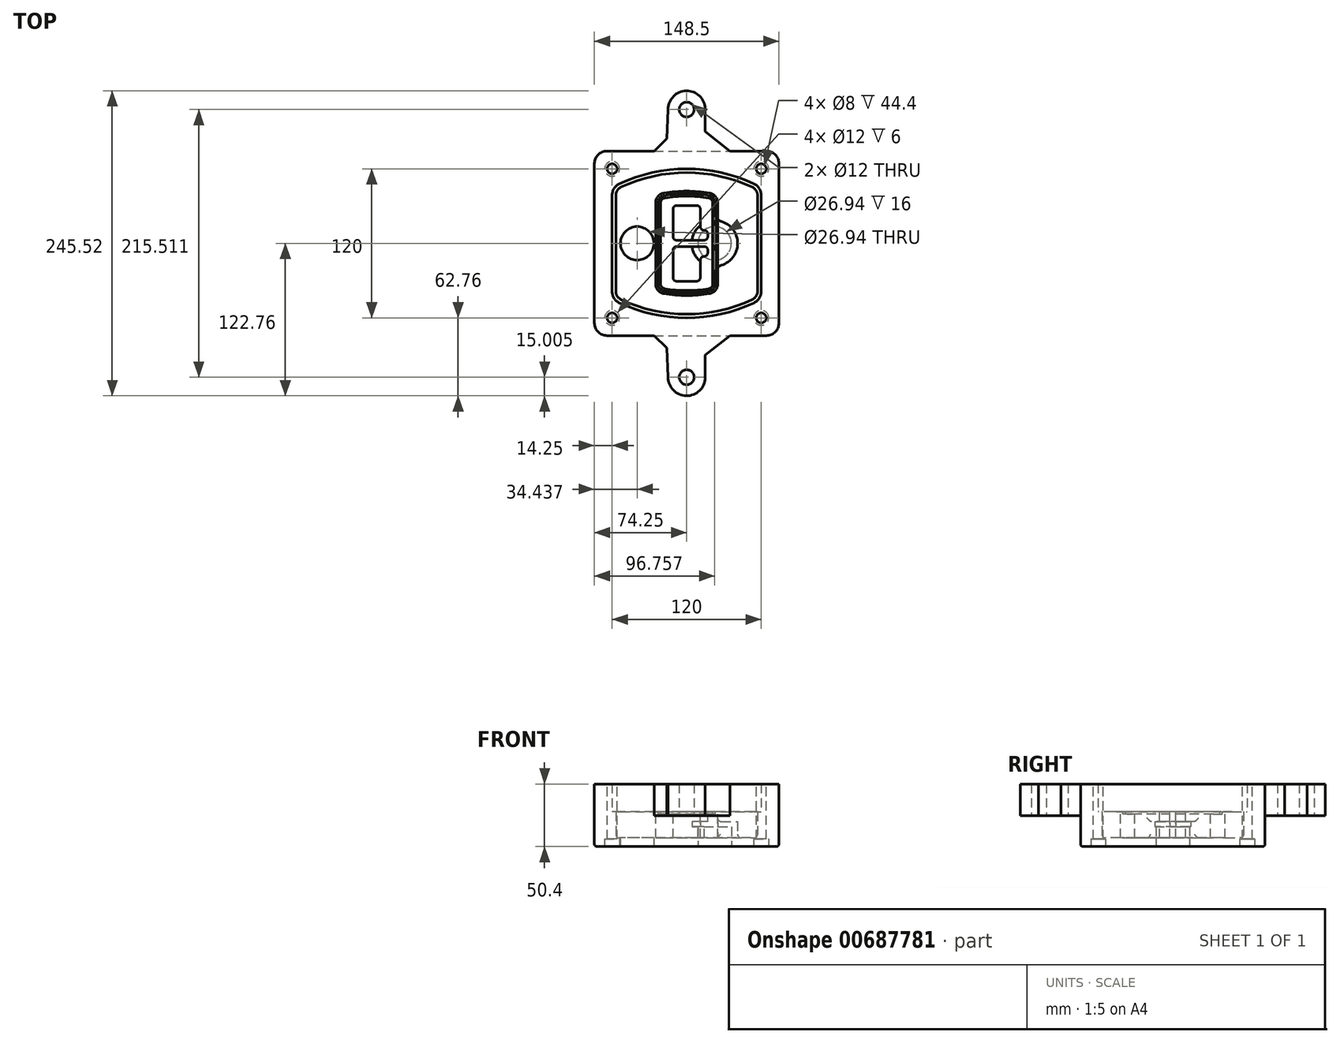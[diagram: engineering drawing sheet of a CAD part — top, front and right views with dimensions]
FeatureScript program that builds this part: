
annotation { "Feature Type Name" : "Feature", "Feature Type Description" : "" }
export const myFeature = defineFeature(function(context is Context, id is Id, definition is map)
    precondition{}
    {
        {
            var Q0;
            Q0=qCreatedBy(makeId("Top.planeOp"),FACE);
            var sketch = newSketch(context, id + "F0", { "sketchPlane" : qUnion([Q0])});
            skPoint(sketch, "E0.rect.middle", {"position": v(0, 0) * mm});
            skLineSegment(sketch, "E1.bottom", {"start": v(-64.25, -74.25) * mm, "end": v(64.25, -74.25) * mm});
            skLineSegment(sketch, "E1.top", {"start": v(-64.25, 74.25) * mm, "end": v(64.25, 74.25) * mm});
            skLineSegment(sketch, "E1.left", {"start": v(-74.25, -64.25) * mm, "end": v(-74.25, 64.25) * mm});
            skLineSegment(sketch, "E1.right", {"start": v(74.25, -64.25) * mm, "end": v(74.25, 64.25) * mm});
            skLineSegment(sketch, "E2", {"start": v(-74.25, 74.25) * mm, "end": v(74.25, -74.25) * mm, "construction": true});
            skLineSegment(sketch, "E3", {"start": v(74.25, 74.25) * mm, "end": v(-74.25, -74.25) * mm, "construction": true});
            skCircle(sketch, "E4", {"center": v(-60, 60) * mm, "radius": 4 * mm});
            skCircle(sketch, "E5", {"center": v(60, 60) * mm, "radius": 4 * mm});
            skCircle(sketch, "E6", {"center": v(60, -60) * mm, "radius": 4 * mm});
            skCircle(sketch, "E7", {"center": v(-60, -60) * mm, "radius": 4 * mm});
            skLineSegment(sketch, "E8", {"start": v(-60, 60) * mm, "end": v(60, 60) * mm, "construction": true});
            skLineSegment(sketch, "E9", {"start": v(60, 60) * mm, "end": v(60, -60) * mm, "construction": true});
            skLineSegment(sketch, "E10", {"start": v(60, -60) * mm, "end": v(-60, -60) * mm, "construction": true});
            skLineSegment(sketch, "E11", {"start": v(-60, -60) * mm, "end": v(-60, 60) * mm, "construction": true});
            skLineSegment(sketch, "E12", {"start": v(-60, 38.83) * mm, "end": v(-60, -38.83) * mm});
            skLineSegment(sketch, "E13", {"start": v(60, 38.83) * mm, "end": v(60, -38.83) * mm});
            skArc(sketch, "E14", {"start": v(54.26, 47.88) * mm, "mid": v(0, 60) * mm, "end": v(-54.26, 47.88) * mm});
            skArc(sketch, "E15", {"start": v(-54.26, -47.88) * mm, "mid": v(0, -60) * mm, "end": v(54.26, -47.88) * mm});
            skLineSegment(sketch, "E16", {"start": v(-60, 0) * mm, "end": v(60, 0) * mm, "construction": true});
            skPoint(sketch, "E17.visualSharp", {"position": v(-60, -45) * mm});
            skArc(sketch, "E17.filletArc", {"start": v(-60, -38.83) * mm, "mid": v(-58.44, -44.2) * mm, "end": v(-54.26, -47.88) * mm});
            skPoint(sketch, "E18.visualSharp", {"position": v(-60, 45) * mm});
            skArc(sketch, "E18.filletArc", {"start": v(-54.26, 47.88) * mm, "mid": v(-58.44, 44.2) * mm, "end": v(-60, 38.83) * mm});
            skPoint(sketch, "E19.visualSharp", {"position": v(60, 45) * mm});
            skArc(sketch, "E19.filletArc", {"start": v(60, 38.83) * mm, "mid": v(58.44, 44.2) * mm, "end": v(54.26, 47.88) * mm});
            skPoint(sketch, "E20.visualSharp", {"position": v(60, -45) * mm});
            skArc(sketch, "E20.filletArc", {"start": v(54.26, -47.88) * mm, "mid": v(58.44, -44.2) * mm, "end": v(60, -38.83) * mm});
            skPoint(sketch, "E21.visualSharp", {"position": v(-74.25, 74.25) * mm});
            skArc(sketch, "E21.filletArc", {"start": v(-64.25, 74.25) * mm, "mid": v(-71.32, 71.32) * mm, "end": v(-74.25, 64.25) * mm});
            skPoint(sketch, "E22.visualSharp", {"position": v(74.25, 74.25) * mm});
            skArc(sketch, "E22.filletArc", {"start": v(74.25, 64.25) * mm, "mid": v(71.32, 71.32) * mm, "end": v(64.25, 74.25) * mm});
            skPoint(sketch, "E23.visualSharp", {"position": v(74.25, -74.25) * mm});
            skArc(sketch, "E23.filletArc", {"start": v(64.25, -74.25) * mm, "mid": v(71.32, -71.32) * mm, "end": v(74.25, -64.25) * mm});
            skPoint(sketch, "E24.visualSharp", {"position": v(-74.25, -74.25) * mm});
            skArc(sketch, "E24.filletArc", {"start": v(-74.25, -64.25) * mm, "mid": v(-71.32, -71.32) * mm, "end": v(-64.25, -74.25) * mm});
            skArc(sketch, "E25.0", {"start": v(57, 38.83) * mm, "mid": v(55.9, 42.58) * mm, "end": v(52.98, 45.17) * mm});
            skLineSegment(sketch, "E25.1", {"start": v(57, 38.83) * mm, "end": v(57, -38.83) * mm});
            skArc(sketch, "E25.2", {"start": v(52.98, -45.17) * mm, "mid": v(55.9, -42.58) * mm, "end": v(57, -38.83) * mm});
            skArc(sketch, "E25.3", {"start": v(-52.98, -45.17) * mm, "mid": v(0, -57) * mm, "end": v(52.98, -45.17) * mm});
            skArc(sketch, "E25.4", {"start": v(-57, -38.83) * mm, "mid": v(-55.9, -42.58) * mm, "end": v(-52.98, -45.17) * mm});
            skArc(sketch, "E25.5", {"start": v(52.98, 45.17) * mm, "mid": v(0, 57) * mm, "end": v(-52.98, 45.17) * mm});
            skLineSegment(sketch, "E25.6", {"start": v(-57, 38.83) * mm, "end": v(-57, -38.83) * mm});
            skArc(sketch, "E25.7", {"start": v(-52.98, 45.17) * mm, "mid": v(-55.9, 42.58) * mm, "end": v(-57, 38.83) * mm});
            skArc(sketch, "E26.0", {"start": v(-55.96, 51.5) * mm, "mid": v(-61.82, 46.33) * mm, "end": v(-64, 38.83) * mm});
            skArc(sketch, "E26.1", {"start": v(55.96, 51.5) * mm, "mid": v(0, 64) * mm, "end": v(-55.96, 51.5) * mm});
            skArc(sketch, "E26.2", {"start": v(64, 38.83) * mm, "mid": v(61.82, 46.33) * mm, "end": v(55.96, 51.5) * mm});
            skLineSegment(sketch, "E26.3", {"start": v(64, 38.83) * mm, "end": v(64, -38.83) * mm});
            skArc(sketch, "E26.4", {"start": v(55.96, -51.5) * mm, "mid": v(61.82, -46.33) * mm, "end": v(64, -38.83) * mm});
            skLineSegment(sketch, "E26.5", {"start": v(-64, 38.83) * mm, "end": v(-64, -38.83) * mm});
            skArc(sketch, "E26.6", {"start": v(-55.96, -51.5) * mm, "mid": v(0, -64) * mm, "end": v(55.96, -51.5) * mm});
            skArc(sketch, "E26.7", {"start": v(-64, -38.83) * mm, "mid": v(-61.82, -46.33) * mm, "end": v(-55.96, -51.5) * mm});
            skSolve(sketch);
        }
        {
            var Q0;
            Q0=makeQuery(id+"F0.imprint","IMPRINT",FACE,{"disambiguationData":[TD([[makeQuery(id+"F0.imprint","IMPRINT",EDGE,{"derivedFrom":sQuery(id+"F0.wireOp",EDGE,"E1.bottom")}),1.0]])]});
            var Q1;
            Q1=makeQuery(id+"F0.imprint","IMPRINT",FACE,{"disambiguationData":[TD([[makeQuery(id+"F0.imprint","IMPRINT",EDGE,{"derivedFrom":sQuery(id+"F0.wireOp",EDGE,"E12")}),1.0]])]});
            var Q2;
            Q2=makeQuery(id+"F0.imprint","IMPRINT",FACE,{"disambiguationData":[TD([[makeQuery(id+"F0.imprint","IMPRINT",EDGE,{"derivedFrom":sQuery(id+"F0.wireOp",EDGE,"E25.0")}),1.0]])]});
            var Q3;
            Q3=makeQuery(id+"F0.imprint","IMPRINT",FACE,{"disambiguationData":[TD([[makeQuery(id+"F0.imprint","IMPRINT",EDGE,{"derivedFrom":sQuery(id+"F0.wireOp",EDGE,"E12")}),-1.0]])]});
            extrude(context, id + "F1", {"entities" : qUnion([Q0, Q1, Q2, Q3]), "oppositeDirection" : true, "depth" : 25 * mm});
        }
        {
            var Q0;
            Q0=makeQuery(id+"F0.imprint","IMPRINT",FACE,{"disambiguationData":[TD([[makeQuery(id+"F0.imprint","IMPRINT",EDGE,{"derivedFrom":sQuery(id+"F0.wireOp",EDGE,"E12")}),1.0]])]});
            extrude(context, id + "F2", {"entities" : qUnion([Q0]), "operationType" : NewBodyOperationType.ADD, "depth" : 3 * mm});
        }
        {
            var Q0;
            Q0=makeQuery(id+"F0.imprint","IMPRINT",FACE,{"disambiguationData":[TD([[makeQuery(id+"F0.imprint","IMPRINT",EDGE,{"derivedFrom":sQuery(id+"F0.wireOp",EDGE,"E25.0")}),1.0]])]});
            extrude(context, id + "F3", {"entities" : qUnion([Q0]), "operationType" : NewBodyOperationType.REMOVE, "oppositeDirection" : true, "depth" : 18 * mm});
        }
        {
            var Q0;
            Q0=makeQuery(id+"F2.opExtrude","CAP_FACE",FACE,{"disambiguationData":[OSD([sQuery(id+"F0.wireOp",EDGE,"E12"),sQuery(id+"F0.wireOp",EDGE,"E13"),sQuery(id+"F0.wireOp",EDGE,"E14"),sQuery(id+"F0.wireOp",EDGE,"E15"),sQuery(id+"F0.wireOp",EDGE,"E17.filletArc"),sQuery(id+"F0.wireOp",EDGE,"E18.filletArc"),sQuery(id+"F0.wireOp",EDGE,"E19.filletArc"),sQuery(id+"F0.wireOp",EDGE,"E20.filletArc"),sQuery(id+"F0.wireOp",EDGE,"E25.0"),sQuery(id+"F0.wireOp",EDGE,"E25.1"),sQuery(id+"F0.wireOp",EDGE,"E25.2"),sQuery(id+"F0.wireOp",EDGE,"E25.3"),sQuery(id+"F0.wireOp",EDGE,"E25.4"),sQuery(id+"F0.wireOp",EDGE,"E25.5"),sQuery(id+"F0.wireOp",EDGE,"E25.6"),sQuery(id+"F0.wireOp",EDGE,"E25.7")])],"isStart":false});
            var sketch = newSketch(context, id + "F4", { "sketchPlane" : qUnion([Q0])});
            skArc(sketch, "E27.0", {"start": v(-18.34, -40.45) * mm, "mid": v(0, -42) * mm, "end": v(18.34, -40.45) * mm});
            skArc(sketch, "E28.0", {"start": v(18.34, 40.45) * mm, "mid": v(0, 42) * mm, "end": v(-18.34, 40.45) * mm});
            skLineSegment(sketch, "E29", {"start": v(-25, 32.57) * mm, "end": v(-25, -32.57) * mm});
            skLineSegment(sketch, "E30", {"start": v(25, 32.57) * mm, "end": v(25, -32.57) * mm});
            skLineSegment(sketch, "E31", {"start": v(-25, 39.1) * mm, "end": v(25, 39.1) * mm, "construction": true});
            skLineSegment(sketch, "E32", {"start": v(-25, -39.1) * mm, "end": v(25, -39.1) * mm, "construction": true});
            skPoint(sketch, "E33.visualSharp", {"position": v(-25, 39.1) * mm});
            skArc(sketch, "E33.filletArc", {"start": v(-18.34, 40.45) * mm, "mid": v(-23.11, 37.73) * mm, "end": v(-25, 32.57) * mm});
            skPoint(sketch, "E34.visualSharp", {"position": v(25, 39.1) * mm});
            skArc(sketch, "E34.filletArc", {"start": v(25, 32.57) * mm, "mid": v(23.11, 37.73) * mm, "end": v(18.34, 40.45) * mm});
            skPoint(sketch, "E35.visualSharp", {"position": v(25, -39.1) * mm});
            skArc(sketch, "E35.filletArc", {"start": v(18.34, -40.45) * mm, "mid": v(23.11, -37.73) * mm, "end": v(25, -32.57) * mm});
            skPoint(sketch, "E36.visualSharp", {"position": v(-25, -39.1) * mm});
            skArc(sketch, "E36.filletArc", {"start": v(-25, -32.57) * mm, "mid": v(-23.11, -37.73) * mm, "end": v(-18.34, -40.45) * mm});
            skArc(sketch, "E37.0", {"start": v(52.98, 45.17) * mm, "mid": v(0, 57) * mm, "end": v(-52.98, 45.17) * mm});
            skArc(sketch, "E37.1", {"start": v(-52.98, 45.17) * mm, "mid": v(-55.9, 42.58) * mm, "end": v(-57, 38.83) * mm});
            skLineSegment(sketch, "E37.2", {"start": v(-57, 38.83) * mm, "end": v(-57, -38.83) * mm});
            skArc(sketch, "E37.3", {"start": v(-57, -38.83) * mm, "mid": v(-55.9, -42.58) * mm, "end": v(-52.98, -45.17) * mm});
            skArc(sketch, "E37.4", {"start": v(-52.98, -45.17) * mm, "mid": v(0, -57) * mm, "end": v(52.98, -45.17) * mm});
            skArc(sketch, "E37.5", {"start": v(52.98, -45.17) * mm, "mid": v(55.9, -42.58) * mm, "end": v(57, -38.83) * mm});
            skLineSegment(sketch, "E37.6", {"start": v(57, 38.83) * mm, "end": v(57, -38.83) * mm});
            skArc(sketch, "E37.7", {"start": v(57, 38.83) * mm, "mid": v(55.9, 42.58) * mm, "end": v(52.98, 45.17) * mm});
            skLineSegment(sketch, "E38.0", {"start": v(23, 32.57) * mm, "end": v(23, -32.57) * mm});
            skArc(sketch, "E38.1", {"start": v(18, -38.48) * mm, "mid": v(21.58, -36.44) * mm, "end": v(23, -32.57) * mm});
            skArc(sketch, "E38.2", {"start": v(-18, -38.48) * mm, "mid": v(0, -40) * mm, "end": v(18, -38.48) * mm});
            skArc(sketch, "E38.3", {"start": v(-23, -32.57) * mm, "mid": v(-21.58, -36.44) * mm, "end": v(-18, -38.48) * mm});
            skLineSegment(sketch, "E38.4", {"start": v(-23, 32.57) * mm, "end": v(-23, -32.57) * mm});
            skArc(sketch, "E38.5", {"start": v(23, 32.57) * mm, "mid": v(21.58, 36.44) * mm, "end": v(18, 38.48) * mm});
            skArc(sketch, "E38.6", {"start": v(-18, 38.48) * mm, "mid": v(-21.58, 36.44) * mm, "end": v(-23, 32.57) * mm});
            skArc(sketch, "E38.7", {"start": v(18, 38.48) * mm, "mid": v(0, 40) * mm, "end": v(-18, 38.48) * mm});
            skArc(sketch, "E39.0", {"start": v(21, 32.57) * mm, "mid": v(20.06, 35.15) * mm, "end": v(17.67, 36.5) * mm});
            skLineSegment(sketch, "E39.1", {"start": v(21, 32.57) * mm, "end": v(21, -32.57) * mm});
            skArc(sketch, "E39.2", {"start": v(17.67, -36.5) * mm, "mid": v(20.06, -35.15) * mm, "end": v(21, -32.57) * mm});
            skArc(sketch, "E39.3", {"start": v(-17.67, -36.5) * mm, "mid": v(0, -38) * mm, "end": v(17.67, -36.5) * mm});
            skArc(sketch, "E39.4", {"start": v(-21, -32.57) * mm, "mid": v(-20.06, -35.15) * mm, "end": v(-17.67, -36.5) * mm});
            skArc(sketch, "E39.5", {"start": v(17.67, 36.5) * mm, "mid": v(0, 38) * mm, "end": v(-17.67, 36.5) * mm});
            skLineSegment(sketch, "E39.6", {"start": v(-21, 32.57) * mm, "end": v(-21, -32.57) * mm});
            skArc(sketch, "E39.7", {"start": v(-17.67, 36.5) * mm, "mid": v(-20.06, 35.15) * mm, "end": v(-21, 32.57) * mm});
            skLineSegment(sketch, "E40", {"start": v(-25, 0) * mm, "end": v(25, 0) * mm, "construction": true});
            skLineSegment(sketch, "E41", {"start": v(-11, 5.5) * mm, "end": v(-11, 27.5) * mm});
            skLineSegment(sketch, "E42", {"start": v(-8, 30.5) * mm, "end": v(8, 30.5) * mm});
            skLineSegment(sketch, "E43", {"start": v(11, 27.5) * mm, "end": v(11, 13.5) * mm});
            skLineSegment(sketch, "E44", {"start": v(14, 10.5) * mm, "end": v(14, 10.5) * mm});
            skLineSegment(sketch, "E45", {"start": v(17, 7.5) * mm, "end": v(17, 5.5) * mm});
            skLineSegment(sketch, "E46", {"start": v(14, 2.5) * mm, "end": v(-8, 2.5) * mm});
            skPoint(sketch, "E47.visualSharp", {"position": v(-11, 30.5) * mm});
            skArc(sketch, "E47.filletArc", {"start": v(-8, 30.5) * mm, "mid": v(-10.12, 29.62) * mm, "end": v(-11, 27.5) * mm});
            skPoint(sketch, "E48.visualSharp", {"position": v(11, 30.5) * mm});
            skArc(sketch, "E48.filletArc", {"start": v(11, 27.5) * mm, "mid": v(10.12, 29.62) * mm, "end": v(8, 30.5) * mm});
            skPoint(sketch, "E49.visualSharp", {"position": v(11, 10.5) * mm});
            skArc(sketch, "E49.filletArc", {"start": v(11, 13.5) * mm, "mid": v(11.88, 11.38) * mm, "end": v(14, 10.5) * mm});
            skPoint(sketch, "E50.visualSharp", {"position": v(17, 10.5) * mm});
            skArc(sketch, "E50.filletArc", {"start": v(17, 7.5) * mm, "mid": v(16.12, 9.62) * mm, "end": v(14, 10.5) * mm});
            skPoint(sketch, "E51.visualSharp", {"position": v(17, 2.5) * mm});
            skArc(sketch, "E51.filletArc", {"start": v(14, 2.5) * mm, "mid": v(16.12, 3.38) * mm, "end": v(17, 5.5) * mm});
            skPoint(sketch, "E52.visualSharp", {"position": v(-11, 2.5) * mm});
            skArc(sketch, "E52.filletArc", {"start": v(-11, 5.5) * mm, "mid": v(-10.12, 3.38) * mm, "end": v(-8, 2.5) * mm});
            skLineSegment(sketch, "E53.0.MirrorCS", {"start": v(14, -2.5) * mm, "end": v(-8, -2.5) * mm});
            skArc(sketch, "E54.0.MirrorCS", {"start": v(-11, -5.5) * mm, "mid": v(-10.12, -3.38) * mm, "end": v(-8, -2.5) * mm});
            skLineSegment(sketch, "E55.0.MirrorCS", {"start": v(-11, -5.5) * mm, "end": v(-11, -27.5) * mm});
            skArc(sketch, "E56.0.MirrorCS", {"start": v(-8, -30.5) * mm, "mid": v(-10.12, -29.62) * mm, "end": v(-11, -27.5) * mm});
            skLineSegment(sketch, "E57.0.MirrorCS", {"start": v(-8, -30.5) * mm, "end": v(8, -30.5) * mm});
            skArc(sketch, "E58.0.MirrorCS", {"start": v(11, -27.5) * mm, "mid": v(10.12, -29.62) * mm, "end": v(8, -30.5) * mm});
            skLineSegment(sketch, "E59.0.MirrorCS", {"start": v(11, -27.5) * mm, "end": v(11, -13.5) * mm});
            skArc(sketch, "E60.0.MirrorCS", {"start": v(11, -13.5) * mm, "mid": v(11.88, -11.38) * mm, "end": v(14, -10.5) * mm});
            skArc(sketch, "E61.0.MirrorCS", {"start": v(17, -7.5) * mm, "mid": v(16.12, -9.62) * mm, "end": v(14, -10.5) * mm});
            skLineSegment(sketch, "E62.0.MirrorCS", {"start": v(17, -7.5) * mm, "end": v(17, -5.5) * mm});
            skArc(sketch, "E63.0.MirrorCS", {"start": v(14, -2.5) * mm, "mid": v(16.12, -3.38) * mm, "end": v(17, -5.5) * mm});
            skSolve(sketch);
        }
        {
            var Q0;
            Q0=makeQuery(id+"F4.imprint","IMPRINT",FACE,{"disambiguationData":[TD([[makeQuery(id+"F4.imprint","IMPRINT",EDGE,{"derivedFrom":sQuery(id+"F4.wireOp",EDGE,"E27.0")}),1.0]])]});
            var Q1;
            Q1=makeQuery(id+"F4.imprint","IMPRINT",FACE,{"disambiguationData":[TD([[makeQuery(id+"F4.imprint","IMPRINT",EDGE,{"derivedFrom":sQuery(id+"F4.wireOp",EDGE,"E38.0")}),-1.0]])]});
            var Q2;
            Q2=makeQuery(id+"F4.imprint","IMPRINT",FACE,{"disambiguationData":[TD([[makeQuery(id+"F4.imprint","IMPRINT",EDGE,{"derivedFrom":sQuery(id+"F4.wireOp",EDGE,"E39.0")}),1.0]])]});
            extrude(context, id + "F5", {"entities" : qUnion([Q0, Q1, Q2]), "operationType" : NewBodyOperationType.ADD, "endBound" : BoundingType.UP_TO_NEXT, "oppositeDirection" : true, "depth" : 25 * mm});
        }
        {
            var Q0;
            Q0=makeQuery(id+"F4.imprint","IMPRINT",FACE,{"disambiguationData":[TD([[makeQuery(id+"F4.imprint","IMPRINT",EDGE,{"derivedFrom":sQuery(id+"F4.wireOp",EDGE,"E38.0")}),-1.0]])]});
            extrude(context, id + "F6", {"entities" : qUnion([Q0]), "operationType" : NewBodyOperationType.REMOVE, "oppositeDirection" : true, "depth" : 2 * mm});
        }
        {
            var Q0;
            Q0=makeQuery(id+"F1.opExtrude","CAP_FACE",FACE,{"disambiguationData":[OSD([sQuery(id+"F0.wireOp",EDGE,"E1.bottom"),sQuery(id+"F0.wireOp",EDGE,"E1.top"),sQuery(id+"F0.wireOp",EDGE,"E1.left"),sQuery(id+"F0.wireOp",EDGE,"E1.right"),sQuery(id+"F0.wireOp",EDGE,"E4"),sQuery(id+"F0.wireOp",EDGE,"E5"),sQuery(id+"F0.wireOp",EDGE,"E6"),sQuery(id+"F0.wireOp",EDGE,"E7"),sQuery(id+"F0.wireOp",EDGE,"E21.filletArc"),sQuery(id+"F0.wireOp",EDGE,"E22.filletArc"),sQuery(id+"F0.wireOp",EDGE,"E23.filletArc"),sQuery(id+"F0.wireOp",EDGE,"E24.filletArc")])],"isStart":false});
            var sketch = newSketch(context, id + "F7", { "sketchPlane" : qUnion([Q0])});
            skCircle(sketch, "E64", {"center": v(22.5, 0) * mm, "radius": 13.47 * mm});
            skCircle(sketch, "E65", {"center": v(-39.81, 0) * mm, "radius": 13.47 * mm});
            skLineSegment(sketch, "E66", {"start": v(74.25, 0) * mm, "end": v(-74.25, 0) * mm});
            skCircle(sketch, "E67", {"center": v(22.5, 0) * mm, "radius": 18.47 * mm});
            skCircle(sketch, "E68", {"center": v(60, -60) * mm, "radius": 6 * mm});
            skCircle(sketch, "E69", {"center": v(-60, -60) * mm, "radius": 6 * mm});
            skCircle(sketch, "E70", {"center": v(-60, 60) * mm, "radius": 6 * mm});
            skCircle(sketch, "E71", {"center": v(60, 60) * mm, "radius": 6 * mm});
            skSolve(sketch);
        }
        {
            var Q0;
            {var subQ1=sQuery(id+"F7.wireOp",EDGE,"E66");var subQ4=sQuery(id+"F7.wireOp",EDGE,"E64");var subQ6=makeQuery(id+"F7.imprint","INTERSECT",VERTEX,{"disambiguationData":[OD(0.0)],"derivedFrom":[subQ4,subQ1]});Q0=makeQuery(id+"F7.imprint","IMPRINT",FACE,{"disambiguationData":[TD([[makeQuery(id+"F7.imprint","IMPRINT",EDGE,{"disambiguationData":[TD([[subQ6,-1.0]])],"derivedFrom":subQ4}),-1.0]])]});}
            var Q1;
            {var subQ0=sQuery(id+"F7.wireOp",EDGE,"E66");var subQ1=sQuery(id+"F7.wireOp",EDGE,"E64");var subQ3=makeQuery(id+"F7.imprint","INTERSECT",VERTEX,{"disambiguationData":[OD(0.0)],"derivedFrom":[subQ1,subQ0]});Q1=makeQuery(id+"F7.imprint","IMPRINT",FACE,{"disambiguationData":[TD([[makeQuery(id+"F7.imprint","IMPRINT",EDGE,{"disambiguationData":[TD([[subQ3,-1.0]])],"derivedFrom":subQ1}),1.0]])]});}
            var Q2;
            {var subQ0=sQuery(id+"F7.wireOp",EDGE,"E66");var subQ1=sQuery(id+"F7.wireOp",EDGE,"E64");var subQ3=makeQuery(id+"F7.imprint","INTERSECT",VERTEX,{"disambiguationData":[OD(0.0)],"derivedFrom":[subQ1,subQ0]});Q2=makeQuery(id+"F7.imprint","IMPRINT",FACE,{"disambiguationData":[TD([[makeQuery(id+"F7.imprint","IMPRINT",EDGE,{"disambiguationData":[TD([[subQ3,1.0]])],"derivedFrom":subQ1}),1.0]])]});}
            var Q3;
            {var subQ1=sQuery(id+"F7.wireOp",EDGE,"E66");var subQ4=sQuery(id+"F7.wireOp",EDGE,"E64");var subQ6=makeQuery(id+"F7.imprint","INTERSECT",VERTEX,{"disambiguationData":[OD(0.0)],"derivedFrom":[subQ4,subQ1]});Q3=makeQuery(id+"F7.imprint","IMPRINT",FACE,{"disambiguationData":[TD([[makeQuery(id+"F7.imprint","IMPRINT",EDGE,{"disambiguationData":[TD([[subQ6,1.0]])],"derivedFrom":subQ4}),-1.0]])]});}
            extrude(context, id + "F8", {"entities" : qUnion([Q0, Q1, Q2, Q3]), "operationType" : NewBodyOperationType.ADD, "oppositeDirection" : true, "depth" : 20 * mm});
        }
        {
            var Q0;
            {var subQ0=sQuery(id+"F7.wireOp",EDGE,"E66");var subQ1=sQuery(id+"F7.wireOp",EDGE,"E64");var subQ3=makeQuery(id+"F7.imprint","INTERSECT",VERTEX,{"disambiguationData":[OD(0.0)],"derivedFrom":[subQ1,subQ0]});Q0=makeQuery(id+"F7.imprint","IMPRINT",FACE,{"disambiguationData":[TD([[makeQuery(id+"F7.imprint","IMPRINT",EDGE,{"disambiguationData":[TD([[subQ3,-1.0]])],"derivedFrom":subQ1}),1.0]])]});}
            var Q1;
            {var subQ0=sQuery(id+"F7.wireOp",EDGE,"E66");var subQ1=sQuery(id+"F7.wireOp",EDGE,"E64");var subQ3=makeQuery(id+"F7.imprint","INTERSECT",VERTEX,{"disambiguationData":[OD(0.0)],"derivedFrom":[subQ1,subQ0]});Q1=makeQuery(id+"F7.imprint","IMPRINT",FACE,{"disambiguationData":[TD([[makeQuery(id+"F7.imprint","IMPRINT",EDGE,{"disambiguationData":[TD([[subQ3,1.0]])],"derivedFrom":subQ1}),1.0]])]});}
            extrude(context, id + "F9", {"entities" : qUnion([Q0, Q1]), "operationType" : NewBodyOperationType.REMOVE, "oppositeDirection" : true, "depth" : 16 * mm});
        }
        {
            var Q0;
            {var subQ0=sQuery(id+"F7.wireOp",EDGE,"E66");var subQ1=sQuery(id+"F7.wireOp",EDGE,"E65");var subQ3=makeQuery(id+"F7.imprint","INTERSECT",VERTEX,{"disambiguationData":[OD(0.0)],"derivedFrom":[subQ1,subQ0]});Q0=makeQuery(id+"F7.imprint","IMPRINT",FACE,{"disambiguationData":[TD([[makeQuery(id+"F7.imprint","IMPRINT",EDGE,{"disambiguationData":[TD([[subQ3,-1.0]])],"derivedFrom":subQ1}),1.0]])]});}
            var Q1;
            {var subQ0=sQuery(id+"F7.wireOp",EDGE,"E66");var subQ1=sQuery(id+"F7.wireOp",EDGE,"E65");var subQ3=makeQuery(id+"F7.imprint","INTERSECT",VERTEX,{"disambiguationData":[OD(0.0)],"derivedFrom":[subQ1,subQ0]});Q1=makeQuery(id+"F7.imprint","IMPRINT",FACE,{"disambiguationData":[TD([[makeQuery(id+"F7.imprint","IMPRINT",EDGE,{"disambiguationData":[TD([[subQ3,1.0]])],"derivedFrom":subQ1}),1.0]])]});}
            extrude(context, id + "F10", {"entities" : qUnion([Q0, Q1]), "operationType" : NewBodyOperationType.REMOVE, "oppositeDirection" : true, "depth" : 25 * mm});
        }
        {
            var Q0;
            Q0=makeQuery(id+"F7.imprint","IMPRINT",FACE,{"disambiguationData":[TD([[makeQuery(id+"F7.imprint","IMPRINT",EDGE,{"derivedFrom":sQuery(id+"F7.wireOp",EDGE,"E68")}),1.0]])]});
            var Q1;
            Q1=makeQuery(id+"F7.imprint","IMPRINT",FACE,{"disambiguationData":[TD([[makeQuery(id+"F7.imprint","IMPRINT",EDGE,{"derivedFrom":makeQuery(id+"F1.opExtrude","CAP_EDGE",EDGE,{"disambiguationData":[OSD([sQuery(id+"F0.wireOp",EDGE,"E5")])],"isStart":false})}),-1.0]])]});
            var Q2;
            Q2=makeQuery(id+"F7.imprint","IMPRINT",FACE,{"disambiguationData":[TD([[makeQuery(id+"F7.imprint","IMPRINT",EDGE,{"derivedFrom":sQuery(id+"F7.wireOp",EDGE,"E69")}),1.0]])]});
            var Q3;
            Q3=makeQuery(id+"F7.imprint","IMPRINT",FACE,{"disambiguationData":[TD([[makeQuery(id+"F7.imprint","IMPRINT",EDGE,{"derivedFrom":makeQuery(id+"F1.opExtrude","CAP_EDGE",EDGE,{"disambiguationData":[OSD([sQuery(id+"F0.wireOp",EDGE,"E4")])],"isStart":false})}),-1.0]])]});
            var Q4;
            Q4=makeQuery(id+"F7.imprint","IMPRINT",FACE,{"disambiguationData":[TD([[makeQuery(id+"F7.imprint","IMPRINT",EDGE,{"derivedFrom":sQuery(id+"F7.wireOp",EDGE,"E70")}),1.0]])]});
            var Q5;
            Q5=makeQuery(id+"F7.imprint","IMPRINT",FACE,{"disambiguationData":[TD([[makeQuery(id+"F7.imprint","IMPRINT",EDGE,{"derivedFrom":makeQuery(id+"F1.opExtrude","CAP_EDGE",EDGE,{"disambiguationData":[OSD([sQuery(id+"F0.wireOp",EDGE,"E7")])],"isStart":false})}),-1.0]])]});
            var Q6;
            Q6=makeQuery(id+"F7.imprint","IMPRINT",FACE,{"disambiguationData":[TD([[makeQuery(id+"F7.imprint","IMPRINT",EDGE,{"derivedFrom":sQuery(id+"F7.wireOp",EDGE,"E71")}),1.0]])]});
            var Q7;
            Q7=makeQuery(id+"F7.imprint","IMPRINT",FACE,{"disambiguationData":[TD([[makeQuery(id+"F7.imprint","IMPRINT",EDGE,{"derivedFrom":makeQuery(id+"F1.opExtrude","CAP_EDGE",EDGE,{"disambiguationData":[OSD([sQuery(id+"F0.wireOp",EDGE,"E6")])],"isStart":false})}),-1.0]])]});
            extrude(context, id + "F11", {"entities" : qUnion([Q0, Q1, Q2, Q3, Q4, Q5, Q6, Q7]), "operationType" : NewBodyOperationType.REMOVE, "oppositeDirection" : true, "depth" : 6 * mm});
        }
        {
            var Q0;
            Q0=makeQuery(id+"F9.boolean.opBoolean","COPY",FACE,{"derivedFrom":makeQuery(id+"F9.opExtrude","CAP_FACE",FACE,{"disambiguationData":[OSD([sQuery(id+"F7.wireOp",EDGE,"E64")])],"isStart":false})});
            var sketch = newSketch(context, id + "F12", { "sketchPlane" : qUnion([Q0])});
            skArc(sketch, "E72.0", {"start": v(11, 14.45) * mm, "mid": v(6.45, 9.13) * mm, "end": v(4.2, 2.5) * mm});
            skArc(sketch, "E72.1", {"start": v(4.2, -2.5) * mm, "mid": v(6.45, -9.13) * mm, "end": v(11, -14.45) * mm});
            skLineSegment(sketch, "E73", {"start": v(4.2, -2.5) * mm, "end": v(14, -2.5) * mm});
            skLineSegment(sketch, "E74.0", {"start": v(14, 2.5) * mm, "end": v(4.2, 2.5) * mm});
            skArc(sketch, "E74.1", {"start": v(14, 2.5) * mm, "mid": v(16.12, 3.38) * mm, "end": v(17, 5.5) * mm});
            skLineSegment(sketch, "E74.2", {"start": v(17, 7.5) * mm, "end": v(17, 5.5) * mm});
            skArc(sketch, "E74.3", {"start": v(17, 7.5) * mm, "mid": v(16.12, 9.62) * mm, "end": v(14, 10.5) * mm});
            skArc(sketch, "E74.4", {"start": v(11, 13.5) * mm, "mid": v(11.88, 11.38) * mm, "end": v(14, 10.5) * mm});
            skLineSegment(sketch, "E74.5", {"start": v(11, 14.45) * mm, "end": v(11, 13.5) * mm});
            skLineSegment(sketch, "E74.7", {"start": v(14, -2.5) * mm, "end": v(4.2, -2.5) * mm});
            skArc(sketch, "E74.8", {"start": v(14, -2.5) * mm, "mid": v(16.12, -3.38) * mm, "end": v(17, -5.5) * mm});
            skLineSegment(sketch, "E74.9", {"start": v(17, -7.5) * mm, "end": v(17, -5.5) * mm});
            skArc(sketch, "E74.10", {"start": v(17, -7.5) * mm, "mid": v(16.12, -9.62) * mm, "end": v(14, -10.5) * mm});
            skArc(sketch, "E74.11", {"start": v(11, -13.5) * mm, "mid": v(11.88, -11.38) * mm, "end": v(14, -10.5) * mm});
            skLineSegment(sketch, "E74.12", {"start": v(11, -14.45) * mm, "end": v(11, -13.5) * mm});
            skPoint(sketch, "E75.orphan", {"position": v(11, -27.5) * mm});
            skPoint(sketch, "E76.orphan", {"position": v(-8, -2.5) * mm});
            skPoint(sketch, "E77.orphan", {"position": v(-8, 2.5) * mm});
            skPoint(sketch, "E78.orphan", {"position": v(11, 27.5) * mm});
            skSolve(sketch);
        }
        {
            var Q0;
            {var subQ7=sQuery(id+"F12.wireOp",EDGE,"E72.0");var subQ14=sQuery(id+"F12.wireOp",EDGE,"E72.1");var subQ16=sQuery(id+"F12.wireOp",EDGE,"E74.1");var subQ18=sQuery(id+"F12.wireOp",EDGE,"E74.8");Q0=qUnion([makeQuery(id+"F12.imprint","IMPRINT",FACE,{"disambiguationData":[TD([[makeQuery(id+"F12.imprint","IMPRINT",EDGE,{"derivedFrom":subQ7}),1.0]])]}),makeQuery(id+"F12.imprint","IMPRINT",FACE,{"disambiguationData":[TD([[makeQuery(id+"F12.imprint","IMPRINT",EDGE,{"derivedFrom":subQ14}),1.0]])]}),makeQuery(id+"F12.imprint","IMPRINT",FACE,{"disambiguationData":[TD([[makeQuery(id+"F12.imprint","IMPRINT",EDGE,{"derivedFrom":subQ16}),1.0]])]}),makeQuery(id+"F12.imprint","IMPRINT",FACE,{"disambiguationData":[TD([[makeQuery(id+"F12.imprint","IMPRINT",EDGE,{"derivedFrom":subQ18}),-1.0]])]})]);}
            var Q1;
            Q1=makeQuery(id+"F5.boolean.opBoolean","SPLIT",FACE,{"disambiguationData":[TD([makeQuery(id+"F5.opExtrude","SWEPT_FACE",FACE,{"disambiguationData":[OSD([sQuery(id+"F4.wireOp",EDGE,"E41")])]})])],"derivedFrom":makeQuery(id+"F3.boolean.opBoolean","COPY",FACE,{"derivedFrom":makeQuery(id+"F3.opExtrude","CAP_FACE",FACE,{"disambiguationData":[OSD([sQuery(id+"F0.wireOp",EDGE,"E25.0"),sQuery(id+"F0.wireOp",EDGE,"E25.1"),sQuery(id+"F0.wireOp",EDGE,"E25.2"),sQuery(id+"F0.wireOp",EDGE,"E25.3"),sQuery(id+"F0.wireOp",EDGE,"E25.4"),sQuery(id+"F0.wireOp",EDGE,"E25.5"),sQuery(id+"F0.wireOp",EDGE,"E25.6"),sQuery(id+"F0.wireOp",EDGE,"E25.7")])],"isStart":false})})});
            extrude(context, id + "F13", {"entities" : qUnion([Q0]), "operationType" : NewBodyOperationType.REMOVE, "endBound" : BoundingType.UP_TO_SURFACE, "endBoundEntityFace" : qUnion([Q1]), "depth" : 25 * mm});
        }
        {
            var Q0;
            Q0=makeQuery(id+"F3.boolean.opBoolean","COPY",EDGE,{"derivedFrom":makeQuery(id+"F3.opExtrude","CAP_EDGE",EDGE,{"disambiguationData":[OSD([sQuery(id+"F0.wireOp",EDGE,"E25.6")])],"isStart":false})});
            var Q1;
            Q1=makeQuery(id+"F8.boolean.opBoolean","INTERSECT",EDGE,{"derivedFrom":[makeQuery(id+"F5.opExtrude","SWEPT_FACE",FACE,{"disambiguationData":[OSD([sQuery(id+"F4.wireOp",EDGE,"E30")])]}),makeQuery(id+"F8.opExtrude","CAP_FACE",FACE,{"disambiguationData":[OSD([sQuery(id+"F7.wireOp",EDGE,"E67")])],"isStart":false})]});
            var Q2;
            Q2=makeQuery(id+"F8.boolean.opBoolean","INTERSECT",EDGE,{"disambiguationData":[OD(1.0)],"derivedFrom":[makeQuery(id+"F5.opExtrude","SWEPT_FACE",FACE,{"disambiguationData":[OSD([sQuery(id+"F4.wireOp",EDGE,"E30")])]}),makeQuery(id+"F8.opExtrude","SWEPT_FACE",FACE,{"disambiguationData":[OSD([sQuery(id+"F7.wireOp",EDGE,"E67")])]})]});
            var Q3;
            {var subQ0=sQuery(id+"F4.wireOp",EDGE,"E30");Q3=makeQuery(id+"F8.boolean.opBoolean","SPLIT",EDGE,{"disambiguationData":[TD([makeQuery(id+"F5.opExtrude","SWEPT_FACE",FACE,{"disambiguationData":[OSD([sQuery(id+"F4.wireOp",EDGE,"E35.filletArc")])]})])],"derivedFrom":makeQuery(id+"F5.opExtrude","CAP_EDGE",EDGE,{"disambiguationData":[OSD([subQ0])],"isStart":false})});}
            var Q4;
            {var subQ0=sQuery(id+"F0.wireOp",EDGE,"E25.7");var subQ1=sQuery(id+"F0.wireOp",EDGE,"E25.1");var subQ2=sQuery(id+"F0.wireOp",EDGE,"E25.6");var subQ3=sQuery(id+"F0.wireOp",EDGE,"E25.5");var subQ4=sQuery(id+"F0.wireOp",EDGE,"E25.4");var subQ5=sQuery(id+"F0.wireOp",EDGE,"E25.0");var subQ6=sQuery(id+"F0.wireOp",EDGE,"E25.2");var subQ7=sQuery(id+"F0.wireOp",EDGE,"E25.3");Q4=makeQuery(id+"F8.boolean.opBoolean","INTERSECT",EDGE,{"derivedFrom":[makeQuery(id+"F5.boolean.opBoolean","SPLIT",FACE,{"disambiguationData":[TD([makeQuery(id+"F2.opExtrude","SWEPT_FACE",FACE,{"disambiguationData":[OSD([subQ5])]})])],"derivedFrom":makeQuery(id+"F3.boolean.opBoolean","COPY",FACE,{"derivedFrom":makeQuery(id+"F3.opExtrude","CAP_FACE",FACE,{"disambiguationData":[OSD([subQ5,subQ1,subQ6,subQ7,subQ4,subQ3,subQ2,subQ0])],"isStart":false})})}),makeQuery(id+"F8.opExtrude","SWEPT_FACE",FACE,{"disambiguationData":[OSD([sQuery(id+"F7.wireOp",EDGE,"E67")])]})]});}
            var Q5;
            Q5=makeQuery(id+"F8.boolean.opBoolean","INTERSECT",EDGE,{"disambiguationData":[OD(0.0)],"derivedFrom":[makeQuery(id+"F5.opExtrude","SWEPT_FACE",FACE,{"disambiguationData":[OSD([sQuery(id+"F4.wireOp",EDGE,"E30")])]}),makeQuery(id+"F8.opExtrude","SWEPT_FACE",FACE,{"disambiguationData":[OSD([sQuery(id+"F7.wireOp",EDGE,"E67")])]})]});
            fillet(context, id + "F14", {"entities" : qUnion([Q0, Q1, Q2, Q3, Q4, Q5]), "radius" : 3 * mm, "tangentPropagation" : true, "allowEdgeOverflow" : false});
        }
        {
            var Q0;
            Q0=makeQuery(id+"F1.opExtrude","CAP_EDGE",EDGE,{"disambiguationData":[OSD([sQuery(id+"F0.wireOp",EDGE,"E1.bottom")])],"isStart":false});
            fillet(context, id + "F15", {"entities" : qUnion([Q0]), "radius" : 2 * mm, "tangentPropagation" : true, "allowEdgeOverflow" : false});
        }
        {
            var Q0;
            {var subQ0=sQuery(id+"F0.wireOp",EDGE,"E21.filletArc");var subQ1=sQuery(id+"F0.wireOp",EDGE,"E7");var subQ2=sQuery(id+"F0.wireOp",EDGE,"E6");var subQ3=sQuery(id+"F0.wireOp",EDGE,"E5");var subQ4=sQuery(id+"F0.wireOp",EDGE,"E4");var subQ5=sQuery(id+"F0.wireOp",EDGE,"E22.filletArc");var subQ6=sQuery(id+"F0.wireOp",EDGE,"E1.bottom");var subQ7=sQuery(id+"F0.wireOp",EDGE,"E1.right");var subQ8=sQuery(id+"F0.wireOp",EDGE,"E1.top");var subQ9=sQuery(id+"F0.wireOp",EDGE,"E1.left");var subQ10=sQuery(id+"F0.wireOp",EDGE,"E23.filletArc");var subQ11=sQuery(id+"F0.wireOp",EDGE,"E24.filletArc");Q0=makeQuery(id+"F2.boolean.opBoolean","SPLIT",FACE,{"disambiguationData":[TD([makeQuery(id+"F1.opExtrude","SWEPT_FACE",FACE,{"disambiguationData":[OSD([subQ6])]})])],"derivedFrom":makeQuery(id+"F1.opExtrude","CAP_FACE",FACE,{"disambiguationData":[OSD([subQ6,subQ8,subQ9,subQ7,subQ4,subQ3,subQ2,subQ1,subQ0,subQ5,subQ10,subQ11])],"isStart":true})});}
            var sketch = newSketch(context, id + "F16", { "sketchPlane" : qUnion([Q0])});
            skLineSegment(sketch, "E79", {"start": v(0, 74.25) * mm, "end": v(0, 107.76) * mm, "construction": true});
            skCircle(sketch, "E80", {"center": v(0, 107.76) * mm, "radius": 6 * mm});
            skArc(sketch, "E81", {"start": v(-15, 107.76) * mm, "mid": v(-0.24, 122.75) * mm, "end": v(15, 108.24) * mm});
            skLineSegment(sketch, "E82", {"start": v(-26.24, 74.25) * mm, "end": v(-15.93, 84.36) * mm});
            skLineSegment(sketch, "E83", {"start": v(-15.93, 84.36) * mm, "end": v(-15, 107.76) * mm});
            skLineSegment(sketch, "E84", {"start": v(15, 90.09) * mm, "end": v(35, 74.25) * mm});
            skLineSegment(sketch, "E85", {"start": v(35, 74.25) * mm, "end": v(15, 90.09) * mm});
            skLineSegment(sketch, "E86", {"start": v(15, 90.09) * mm, "end": v(15, 108.24) * mm});
            skLineSegment(sketch, "E87", {"start": v(0, 0) * mm, "end": v(-74.25, 0) * mm, "construction": true});
            skLineSegment(sketch, "E88", {"start": v(74.25, 0) * mm, "end": v(0, 0) * mm, "construction": true});
            skLineSegment(sketch, "E89.MirrorCS", {"start": v(-15.93, -84.36) * mm, "end": v(-15, -107.76) * mm});
            skLineSegment(sketch, "E90.MirrorCS", {"start": v(-26.24, -74.25) * mm, "end": v(-15.93, -84.36) * mm});
            skArc(sketch, "E91.MirrorCS", {"start": v(-15, -107.76) * mm, "mid": v(-0.24, -122.75) * mm, "end": v(15, -108.24) * mm});
            skCircle(sketch, "E92.MirrorC", {"center": v(0, -107.76) * mm, "radius": 6 * mm});
            skLineSegment(sketch, "E93.MirrorCS", {"start": v(15, -90.09) * mm, "end": v(35, -74.25) * mm});
            skLineSegment(sketch, "E94.MirrorCS", {"start": v(15, -90.09) * mm, "end": v(15, -108.24) * mm});
            skLineSegment(sketch, "E95.MirrorCS", {"start": v(0, -74.25) * mm, "end": v(0, -107.76) * mm, "construction": true});
            skSolve(sketch);
        }
        {
            var Q0;
            Q0=makeQuery(id+"F16.imprint","IMPRINT",FACE,{"disambiguationData":[TD([[makeQuery(id+"F16.imprint","IMPRINT",EDGE,{"derivedFrom":makeQuery(id+"F1.opExtrude","CAP_EDGE",EDGE,{"disambiguationData":[OSD([sQuery(id+"F0.wireOp",EDGE,"E1.left")])],"isStart":true})}),-1.0]])]});
            var Q1;
            Q1=makeQuery(id+"F16.imprint","IMPRINT",FACE,{"disambiguationData":[TD([[makeQuery(id+"F16.imprint","IMPRINT",EDGE,{"derivedFrom":sQuery(id+"F16.wireOp",EDGE,"E89.MirrorCS")}),1.0]])]});
            var Q2;
            Q2=makeQuery(id+"F16.imprint","IMPRINT",FACE,{"disambiguationData":[TD([[makeQuery(id+"F16.imprint","IMPRINT",EDGE,{"derivedFrom":sQuery(id+"F16.wireOp",EDGE,"E80")}),-1.0]])]});
            extrude(context, id + "F17", {"entities" : qUnion([Q0, Q1, Q2]), "operationType" : NewBodyOperationType.ADD, "depth" : 25.4 * mm, "offsetDistance" : 25.4 * mm});
        }
    });
